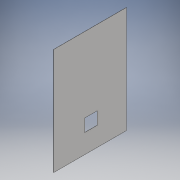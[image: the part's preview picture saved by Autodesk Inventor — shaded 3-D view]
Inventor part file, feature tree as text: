
AUTODESK INVENTOR PART (.ipt)
format: ipt  version: 2018 (Build 220112000, 112)  size: 112,640 bytes
history: native  units: mm
features: extrude x3, sketch x3, projected_geometry x1
ambient origin geometry x8: Origin, YZ Plane, XZ Plane, XY Plane, X Axis, Y Axis, Z Axis, Center Point
bodies: Solid1 (feature_tree)
feature tree (7):
  extrude  "Extrusion1"  Depth=1.6mm
  extrude  "Extrusion2"  Depth=1100.0mm TaperAngle=0.0deg
  extrude  "Extrusion3"  Depth=130.0mm
  sketch  "Sketch1"  dims[d0=700.0mm d1=1.6mm]
  sketch  "Sketch2"  dims[d2=1100.0mm d3=0.0mm d4=50.0mm d5=0.0mm]
  projected_geometry  "Projected Loop1"
  sketch  "Sketch3"  dims[d11=130.0mm d12=130.0mm d13=130.0mm d14=50.0mm d15=0.0mm]
